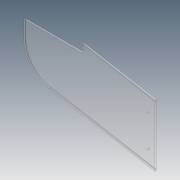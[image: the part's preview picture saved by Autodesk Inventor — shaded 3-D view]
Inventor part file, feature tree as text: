
AUTODESK INVENTOR PART (.ipt)
format: ipt  version: 2012 (Build 160160000, 160)  size: 130,560 bytes
history: native  units: in
note: dims shown in document units (in); Inventor stores cm internally (conversion verified against a paired STEP export)
features: extrude x3, sketch x2, hole x1, pattern_linear x1
ambient origin geometry x8: Origin, YZ Plane, XZ Plane, XY Plane, X Axis, Y Axis, Z Axis, Center Point
bodies: Solid1 (feature_tree)
feature tree (7):
  sketch  "Sketch1"  dims[d0=10.5in d2=0.0687in]
  extrude  "Extrusion1"  Depth=0.0687in
  extrude  "Extrusion2"  Depth=9.3125in
  extrude  "Extrusion3"  Depth=20.75in
  hole  "Hole1"  [1 undecoded]
  pattern_linear  "Rectangular Pattern1"  Spacing1=0.125in  [1 undecoded]
  sketch  "Sketch2"  dims[d3=9.625in d4=9.3125in d5=20.75in d6=0.25in d7=0.0in d8=0.125in d9=0.188in d10=0.188in d11=0.125in d12=0.188in d13=0.125in d14=0.125in d15=0.0in d16=4.5in d17=4.625in d18=4.813in d20=0.265in d21=2.375in d22=5.0in d23=1.1875in d24=1.1875in d25=1.0in d26=0.0in d27=0.5in d28=1.625in d29=0.25in d30=0.75in d31=0.375in d32=0.25in d33=0.5635in d34=1.0in d35=0.8108in d36=1.1811in d38=3.0in]
note: 2 required parameter values undecoded (feature->parameter linkage not recoverable at this tier; creation-order binding heuristic only, values carry confidence <= 0.55)
